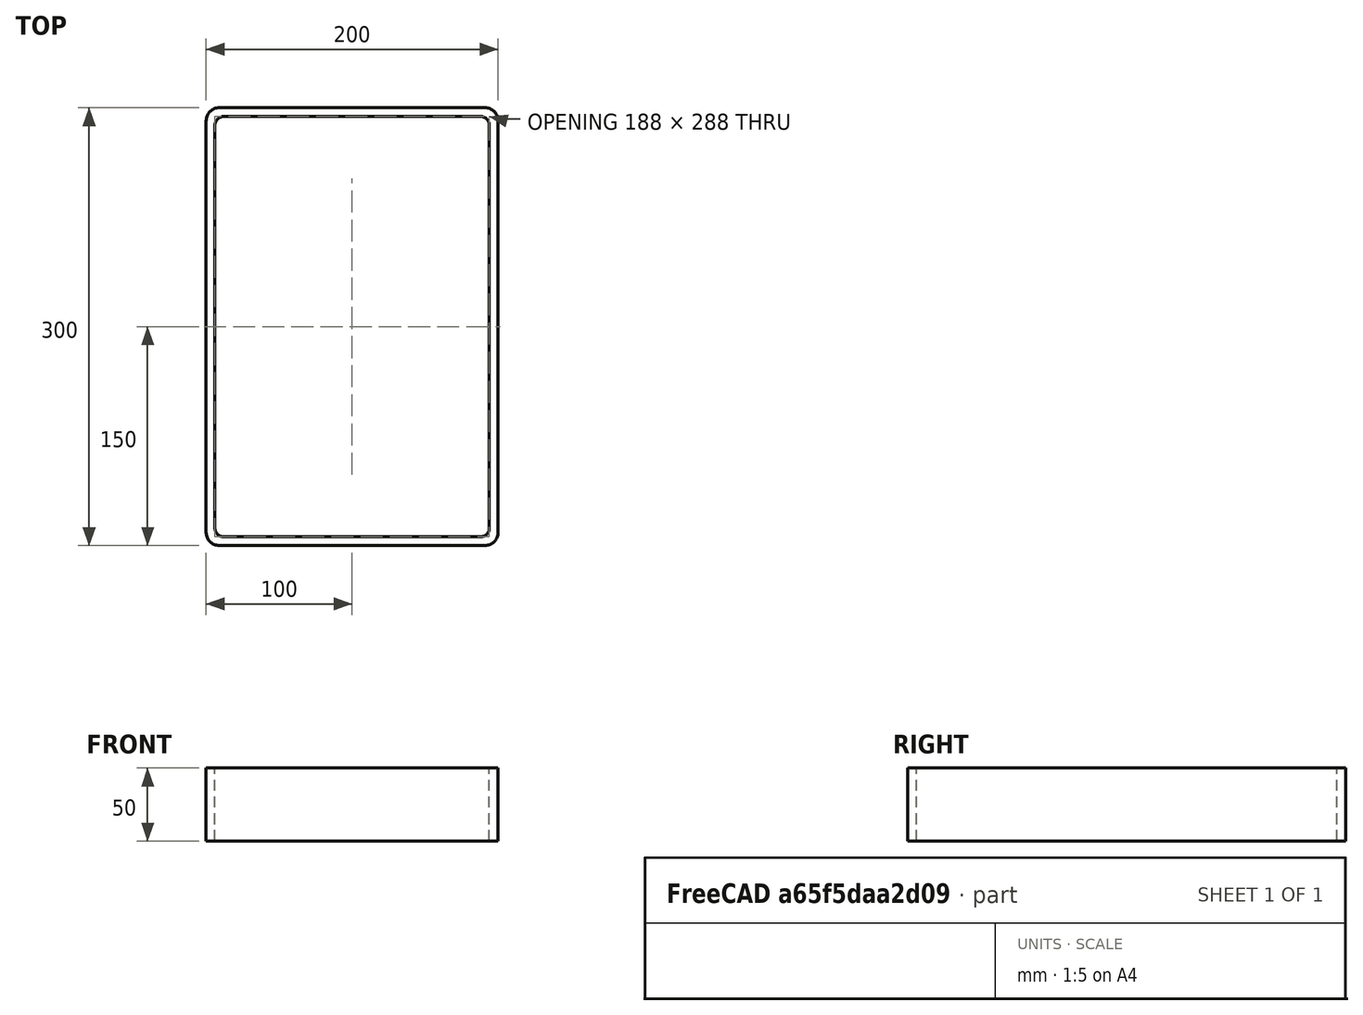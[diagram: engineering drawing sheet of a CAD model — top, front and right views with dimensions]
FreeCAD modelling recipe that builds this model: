
FCSTD DOCUMENT  (FreeCAD 0.15R4671 (Git))
Label: Rectangular hollow section 300x200x6 EN10219 S235JRH
License: All rights reserved
LicenseURL: http://en.wikipedia.org/wiki/All_rights_reserved
objects: Sketcher::SketchObject×1, Part::Extrusion×1
note: 2 computed .brp shape members not serialized (recipe doc carries the construction recipe); baked Part::Feature solids carry a one-line shape summary decoded from their .brp

FEATURE [Sketcher::SketchObject] Sketch
  sketch-geometry (16):
    g0: LineSegment StartX=-88 StartY=144 StartZ=0 EndX=88 EndY=144 EndZ=0
    g1: LineSegment StartX=94 StartY=138 StartZ=0 EndX=94 EndY=-138 EndZ=0
    g2: LineSegment StartX=88 StartY=-144 StartZ=0 EndX=-88 EndY=-144 EndZ=0
    g3: LineSegment StartX=-94 StartY=-138 StartZ=0 EndX=-94 EndY=138 EndZ=0
    g4: LineSegment StartX=-91 StartY=150 StartZ=0 EndX=91 EndY=150 EndZ=0
    g5: LineSegment StartX=100 StartY=141 StartZ=0 EndX=100 EndY=-141 EndZ=0
    g6: LineSegment StartX=91 StartY=-150 StartZ=0 EndX=-91 EndY=-150 EndZ=0
    g7: LineSegment StartX=-100 StartY=-141 StartZ=0 EndX=-100 EndY=141 EndZ=0
    g8: ArcOfCircle CenterX=-88 CenterY=138 CenterZ=0 NormalX=0 NormalY=0 NormalZ=1 Radius=6 StartAngle=1.5708 EndAngle=3.14159
    g9: ArcOfCircle CenterX=88 CenterY=138 CenterZ=0 NormalX=0 NormalY=0 NormalZ=1 Radius=6 StartAngle=0 EndAngle=1.5708
    g10: ArcOfCircle CenterX=88 CenterY=-138 CenterZ=0 NormalX=0 NormalY=0 NormalZ=1 Radius=6 StartAngle=4.71239 EndAngle=6.28319
    g11: ArcOfCircle CenterX=-88 CenterY=-138 CenterZ=0 NormalX=0 NormalY=0 NormalZ=1 Radius=6 StartAngle=3.14159 EndAngle=4.71239
    g12: ArcOfCircle CenterX=91 CenterY=141 CenterZ=0 NormalX=0 NormalY=0 NormalZ=1 Radius=9 StartAngle=0 EndAngle=1.5708
    g13: ArcOfCircle CenterX=91 CenterY=-141 CenterZ=0 NormalX=0 NormalY=0 NormalZ=1 Radius=9 StartAngle=4.71239 EndAngle=6.28319
    g14: ArcOfCircle CenterX=-91 CenterY=-141 CenterZ=0 NormalX=0 NormalY=0 NormalZ=1 Radius=9 StartAngle=3.14159 EndAngle=4.71239
    g15: ArcOfCircle CenterX=-91 CenterY=141 CenterZ=0 NormalX=0 NormalY=0 NormalZ=1 Radius=9 StartAngle=1.5708 EndAngle=3.14159
  constraints (36):
    c: Horizontal(g2)
    c: Vertical(g3)
    c: Horizontal(g6)
    c: Vertical(g7)
    c: Tangent(g3,g8) = 1.5708
    c: Tangent(g0,g8) = 1.5708
    c: Tangent(g0,g9) = 1.5708
    c: Tangent(g1,g9) = 1.5708
    c: Tangent(g1,g10) = 1.5708
    c: Tangent(g2,g10) = 1.5708
    c: Tangent(g2,g11) = 1.5708
    c: Tangent(g3,g11) = 1.5708
    c: Tangent(g4,g12) = 1.5708
    c: Tangent(g5,g12) = 1.5708
    c: Tangent(g5,g13) = 1.5708
    c: Tangent(g6,g13) = 1.5708
    c: Tangent(g6,g14) = 1.5708
    c: Tangent(g7,g14) = 1.5708
    c: Tangent(g7,g15) = 1.5708
    c: Tangent(g4,g15) = 1.5708
    c: Equal(g9,g8)
    c: Equal(g9,g11)
    c: Equal(g9,g10)
    c: Equal(g12,g15)
    c: Equal(g12,g14)
    c: Equal(g12,g13)
    c: Symmetric(g4,g6,g-1)
    c: Symmetric(g7,g5,g-2)
    c: DistanceY(g4,g6) = -300
    c: DistanceX(g7,g5) = 200
    c: Symmetric(g3,g1,g-2)
    c: Symmetric(g0,g2,g-1)
    c: DistanceY(g0,g4) = 6
    c: DistanceX(g5,g1) = -6
    c: Radius(g9) = 6
    c: Radius(g12) = 9
FEATURE [Part::Extrusion] Extrude  label="Rectangular hollow section 300x200x6 EN10219 S235JRH"
  Base = -> Sketch
  Dir = (0,0,50)
  Solid = true
